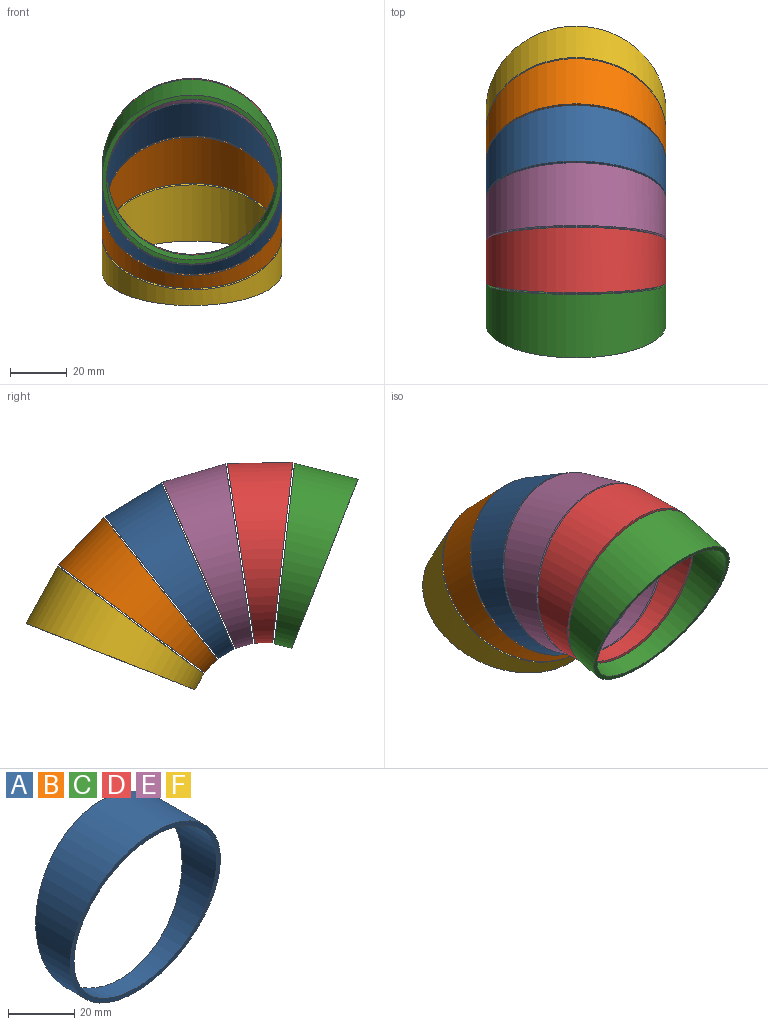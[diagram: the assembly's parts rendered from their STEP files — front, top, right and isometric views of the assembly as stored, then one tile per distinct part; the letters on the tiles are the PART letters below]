
ASSEMBLY  parts=6 mates=5
PART A: 4 faces, bbox 65.3x24.8x65.3 mm
  f0: cylinder r=31.75mm len=63.5mm, axis (0,1,0), area 2934.5mm2, adj f1,f2
  f1: plane 65.26x65.26mm, normal (0,-0.99,-0.13), area 311.4mm2, adj f0,f3
  f2: plane 63.5x63.5mm, normal (0,0.99,-0.13), area 311.4mm2, adj f0,f3
  f3: cylinder r=30.16mm len=60.33mm, axis (0,1,0), area 2787.8mm2, adj f1,f2
PART B: same geometry as A
PART C: same geometry as A
PART D: same geometry as A
PART E: same geometry as A
PART F: same geometry as A
PLACE A rot(axis=(-1,0,0),31.1deg) t=(18.76,47.39,-12.07)mm
PLACE B rot(axis=(-1,0,0),46.1deg) t=(18.76,59.28,-21.57)mm
PLACE C rot(axis=(1,0,0),13.9deg) t=(18.76,3.3,-5.7)mm
PLACE D rot(axis=(-1,0,0),1.1deg) t=(18.76,18.42,-3.7)mm
PLACE E rot(axis=(-1,0,0),16.1deg) t=(18.76,33.46,-5.98)mm
PLACE F rot(axis=(-1,0,0),61.1deg) t=(18.76,68.3,-33.81)mm
MATE cylindrical F.f1 <-> B.f2  axis (0,-0.59,0.81) through (18.76,64.75,-27.37)mm
MATE cylindrical A.f1 <-> E.f2  axis (0,-0.92,0.4) through (18.76,41.1,-8.27)mm
MATE parallel C.f2 <-> D.f1  axis (0,0.99,0.11) through (18.76,10.44,-3.94)mm
MATE cylindrical B.f1 <-> A.f2  axis (0,-0.78,0.62) through (18.76,54.18,-16.26)mm
MATE cylindrical E.f1 <-> D.f2  axis (0,-0.99,0.15) through (18.76,26.39,-3.94)mm
